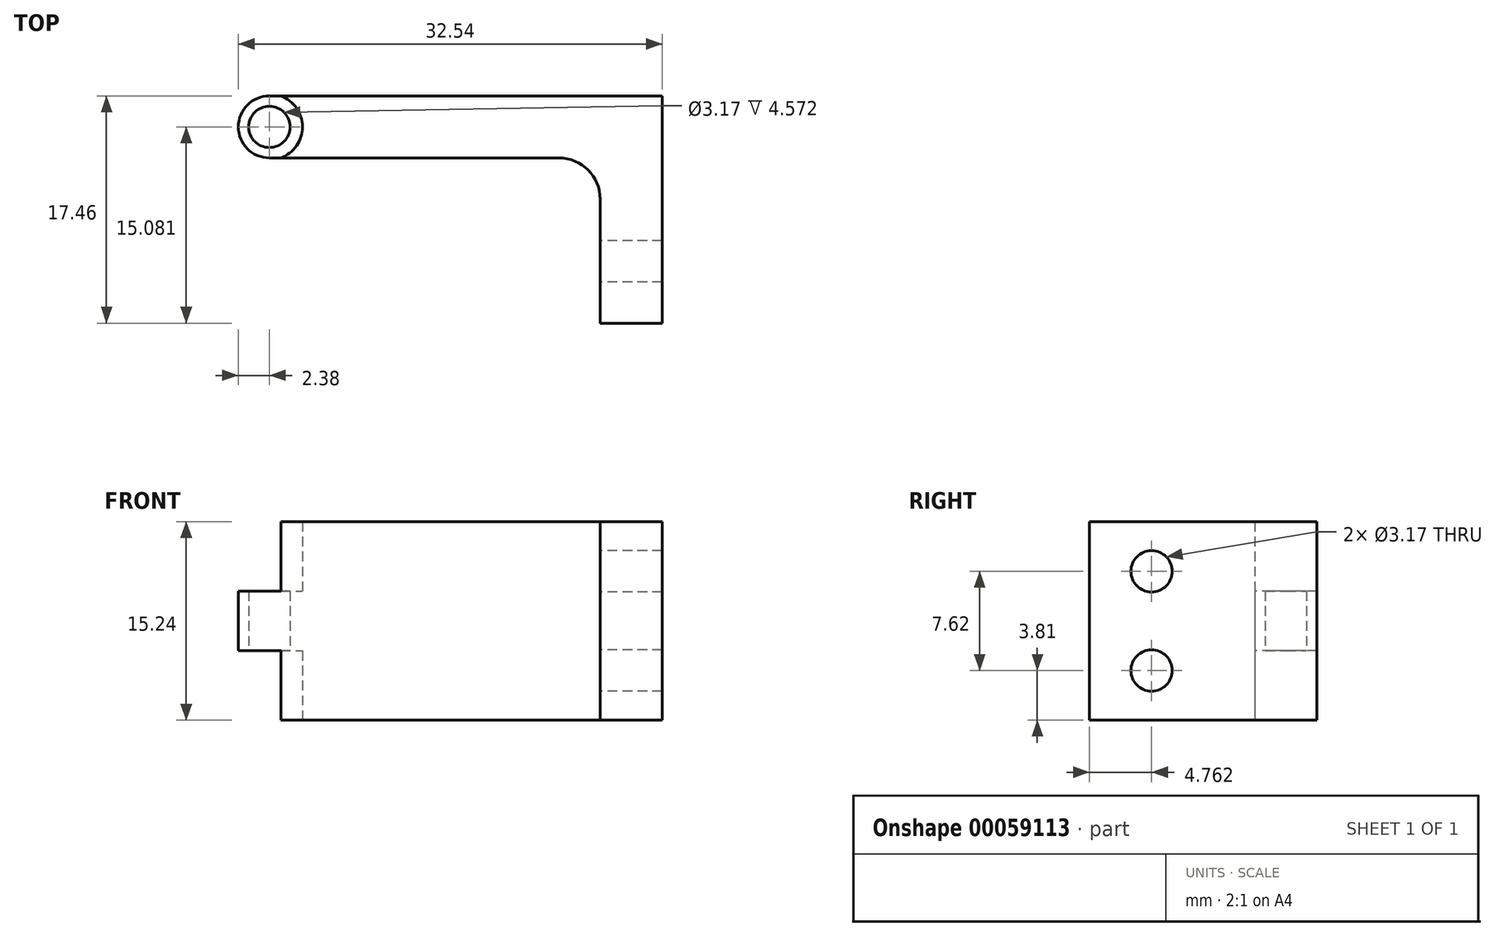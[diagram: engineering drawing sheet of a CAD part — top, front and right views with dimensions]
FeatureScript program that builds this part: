
annotation { "Feature Type Name" : "Feature", "Feature Type Description" : "" }
export const myFeature = defineFeature(function(context is Context, id is Id, definition is map)
    precondition{}
    {
        {
            var Q0;
            Q0=qCreatedBy(makeId("Top.planeOp"),FACE);
            var sketch = newSketch(context, id + "F0", { "sketchPlane" : qUnion([Q0])});
            skLineSegment(sketch, "E0", {"start": v(0, -3.17) * mm, "end": v(0, -12.7) * mm});
            skLineSegment(sketch, "E1", {"start": v(0, -12.7) * mm, "end": v(4.76, -12.7) * mm});
            skLineSegment(sketch, "E2", {"start": v(4.76, -12.7) * mm, "end": v(4.76, 4.76) * mm});
            skLineSegment(sketch, "E3", {"start": v(4.76, 4.76) * mm, "end": v(-25.4, 4.76) * mm});
            skLineSegment(sketch, "E4", {"start": v(-25.4, 0) * mm, "end": v(-3.18, 0) * mm});
            skArc(sketch, "E5", {"start": v(-25.4, 4.76) * mm, "mid": v(-27.78, 2.38) * mm, "end": v(-25.4, 0) * mm});
            skCircle(sketch, "E6", {"center": v(-25.4, 2.38) * mm, "radius": 1.59 * mm});
            skPoint(sketch, "E7.visualSharp", {"position": v(0, 0) * mm});
            skArc(sketch, "E7.filletArc", {"start": v(0, -3.17) * mm, "mid": v(-0.93, -0.93) * mm, "end": v(-3.18, 0) * mm});
            skSolve(sketch);
        }
        {
            var Q0;
            Q0 = qSketchRegion(id + "F0", true);
            extrude(context, id + "F1", {"entities" : qUnion([Q0]), "depth" : 15.24 * mm});
        }
        {
            var Q0;
            Q0=qCreatedBy(makeId("Front.planeOp"),FACE);
            cPlane(context, id + "F2", {"entities" : qUnion([Q0]), "cplaneType" : CPlaneType.OFFSET, "offset" : 2.38 * mm, "oppositeDirection" : true, "width" : 152.4 * mm, "height" : 152.4 * mm});
        }
        {
            var Q0;
            Q0=qCreatedBy(id+"F2.planeOp",FACE);
            var sketch = newSketch(context, id + "F3", { "sketchPlane" : qUnion([Q0])});
            skLineSegment(sketch, "E8.bottom", {"start": v(-27.94, 15.24) * mm, "end": v(-25.4, 15.24) * mm});
            skLineSegment(sketch, "E8.top", {"start": v(-27.94, 9.9) * mm, "end": v(-25.4, 9.9) * mm});
            skLineSegment(sketch, "E8.left", {"start": v(-27.94, 15.24) * mm, "end": v(-27.94, 9.9) * mm});
            skLineSegment(sketch, "E8.right", {"start": v(-25.4, 15.24) * mm, "end": v(-25.4, 9.9) * mm});
            skLineSegment(sketch, "E9.bottom", {"start": v(-27.94, 5.33) * mm, "end": v(-25.4, 5.33) * mm});
            skLineSegment(sketch, "E9.top", {"start": v(-27.94, 0) * mm, "end": v(-25.4, 0) * mm});
            skLineSegment(sketch, "E9.left", {"start": v(-27.94, 5.33) * mm, "end": v(-27.94, 0) * mm});
            skLineSegment(sketch, "E9.right", {"start": v(-25.4, 5.33) * mm, "end": v(-25.4, 0) * mm});
            skSolve(sketch);
        }
        {
            var Q0;
            Q0 = qSketchRegion(id + "F3", true);
            var Q1;
            Q1=sQuery(id+"F3.wireOp",EDGE,"E8.right");
            revolve(context, id + "F4", {"operationType" : NewBodyOperationType.REMOVE, "entities" : qUnion([Q0]), "axis" : qUnion([Q1]), "revolveType" : RevolveType.FULL, "oppositeDirection" : true});
        }
        {
            var Q0;
            Q0=makeQuery(id+"F1.opExtrude","SWEPT_FACE",FACE,{"disambiguationData":[OSD([sQuery(id+"F0.wireOp",EDGE,"E0")])]});
            var sketch = newSketch(context, id + "F5", { "sketchPlane" : qUnion([Q0])});
            skCircle(sketch, "E10", {"center": v(7.94, 11.43) * mm, "radius": 1.59 * mm});
            skPoint(sketch, "E10.centerSnap0", {"position": v(7.94, 15.24) * mm});
            skCircle(sketch, "E11", {"center": v(7.94, 3.81) * mm, "radius": 1.59 * mm});
            skPoint(sketch, "E11.centerSnap0", {"position": v(7.94, 0) * mm});
            skSolve(sketch);
        }
        {
            var Q0;
            Q0 = qSketchRegion(id + "F5", true);
            extrude(context, id + "F6", {"entities" : qUnion([Q0]), "operationType" : NewBodyOperationType.REMOVE, "endBound" : BoundingType.THROUGH_ALL, "oppositeDirection" : true, "depth" : 25.4 * mm});
        }
    });
